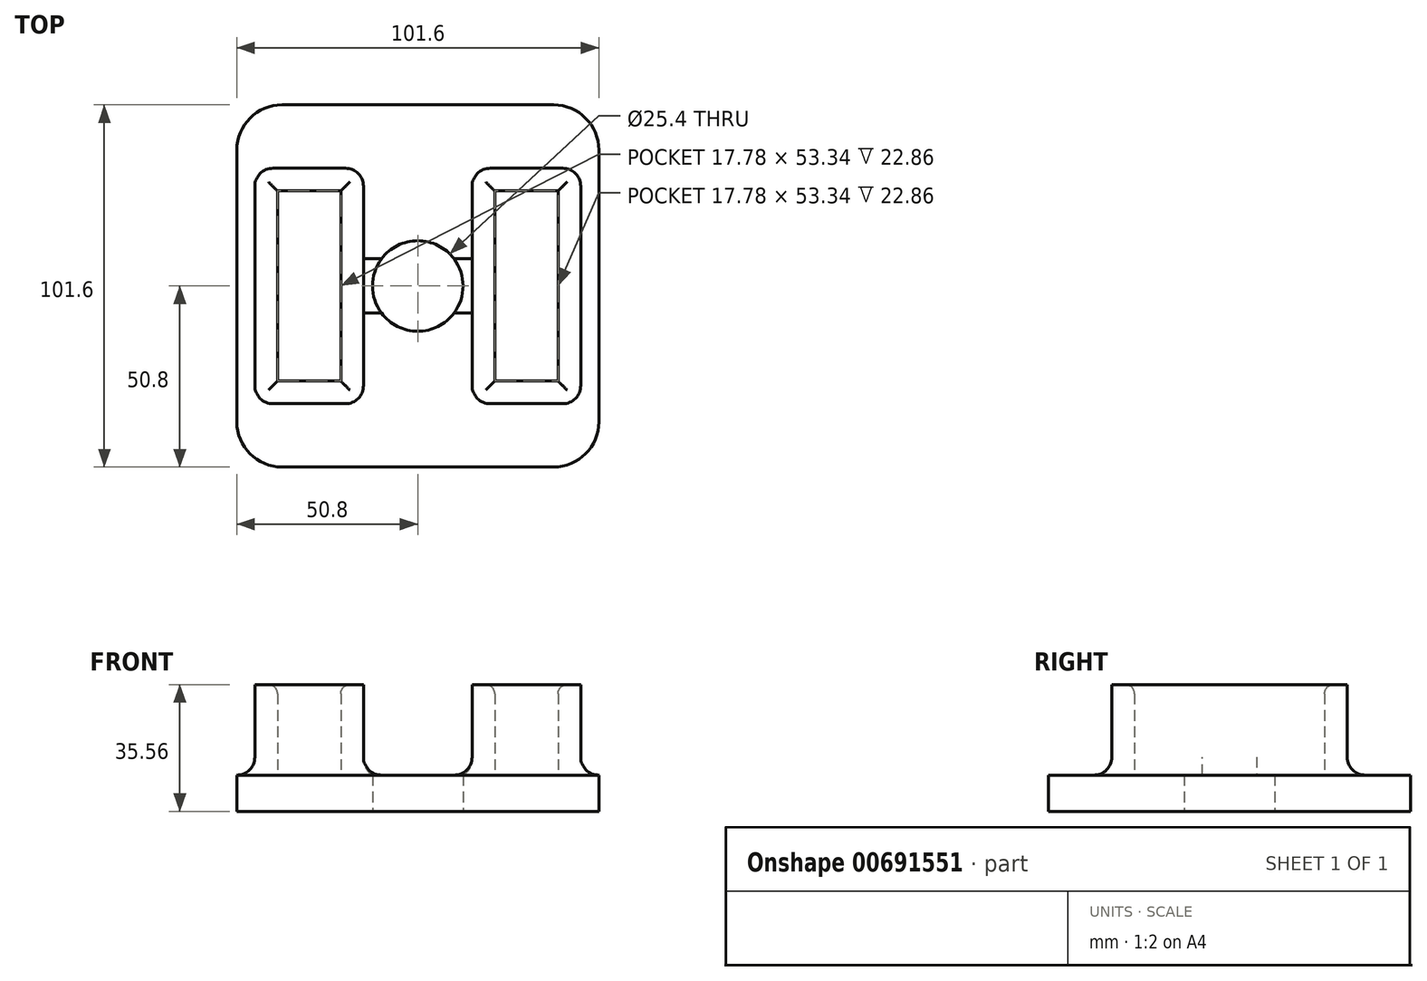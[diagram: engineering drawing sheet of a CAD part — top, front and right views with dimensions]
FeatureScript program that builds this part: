
annotation { "Feature Type Name" : "Feature", "Feature Type Description" : "" }
export const myFeature = defineFeature(function(context is Context, id is Id, definition is map)
    precondition{}
    {
        {
            var Q0;
            Q0=qCreatedBy(makeId("Top.planeOp"),FACE);
            var sketch = newSketch(context, id + "F0", { "sketchPlane" : qUnion([Q0])});
            skLineSegment(sketch, "E0.bottom", {"start": v(50.8, -50.8) * mm, "end": v(-50.8, -50.8) * mm});
            skLineSegment(sketch, "E0.top", {"start": v(50.8, 50.8) * mm, "end": v(-50.8, 50.8) * mm});
            skLineSegment(sketch, "E0.left", {"start": v(50.8, -50.8) * mm, "end": v(50.8, 50.8) * mm});
            skLineSegment(sketch, "E0.right", {"start": v(-50.8, -50.8) * mm, "end": v(-50.8, 50.8) * mm});
            skPoint(sketch, "E0.middle", {"position": v(0, 0) * mm});
            skCircle(sketch, "E1", {"center": v(0, 0) * mm, "radius": 12.7 * mm});
            skSolve(sketch);
        }
        {
            var Q0;
            Q0 = qSketchRegion(id + "F0", true);
            extrude(context, id + "F1", {"entities" : qUnion([Q0]), "depth" : 10.16 * mm, "offsetDistance" : 25.4 * mm});
        }
        {
            var Q0;
            Q0=makeQuery(id+"F1.opExtrude","CAP_FACE",FACE,{"disambiguationData":[OSD([sQuery(id+"F0.wireOp",EDGE,"E0.bottom"),sQuery(id+"F0.wireOp",EDGE,"E0.top"),sQuery(id+"F0.wireOp",EDGE,"E0.left"),sQuery(id+"F0.wireOp",EDGE,"E0.right"),sQuery(id+"F0.wireOp",EDGE,"E1")])],"isStart":false});
            var sketch = newSketch(context, id + "F2", { "sketchPlane" : qUnion([Q0])});
            skLineSegment(sketch, "E2", {"start": v(0, 0) * mm, "end": v(-30.48, 0) * mm});
            skLineSegment(sketch, "E3.bottom", {"start": v(-21.59, -26.67) * mm, "end": v(-39.37, -26.67) * mm});
            skLineSegment(sketch, "E3.top", {"start": v(-21.59, 26.67) * mm, "end": v(-39.37, 26.67) * mm});
            skLineSegment(sketch, "E3.left", {"start": v(-21.59, -26.67) * mm, "end": v(-21.59, 26.67) * mm});
            skLineSegment(sketch, "E3.right", {"start": v(-39.37, -26.67) * mm, "end": v(-39.37, 26.67) * mm});
            skPoint(sketch, "E3.middle", {"position": v(-30.48, 0) * mm});
            skLineSegment(sketch, "E4.bottom", {"start": v(-15.24, -33.02) * mm, "end": v(-45.72, -33.02) * mm});
            skLineSegment(sketch, "E4.top", {"start": v(-15.24, 33.02) * mm, "end": v(-45.72, 33.02) * mm});
            skLineSegment(sketch, "E4.left", {"start": v(-15.24, -33.02) * mm, "end": v(-15.24, 33.02) * mm});
            skLineSegment(sketch, "E4.right", {"start": v(-45.72, -33.02) * mm, "end": v(-45.72, 33.02) * mm});
            skLineSegment(sketch, "E5", {"start": v(0, 0) * mm, "end": v(0, 2.54) * mm});
            skPoint(sketch, "E6.MirrorP", {"position": v(30.48, 0) * mm});
            skLineSegment(sketch, "E7.MirrorCS", {"start": v(21.59, -26.67) * mm, "end": v(39.37, -26.67) * mm});
            skLineSegment(sketch, "E8.MirrorCS", {"start": v(45.72, -33.02) * mm, "end": v(45.72, 33.02) * mm});
            skLineSegment(sketch, "E9.MirrorCS", {"start": v(15.24, -33.02) * mm, "end": v(15.24, 33.02) * mm});
            skLineSegment(sketch, "E10.MirrorCS", {"start": v(21.59, 26.67) * mm, "end": v(39.37, 26.67) * mm});
            skLineSegment(sketch, "E11.MirrorCS", {"start": v(21.59, -26.67) * mm, "end": v(21.59, 26.67) * mm});
            skLineSegment(sketch, "E12.MirrorCS", {"start": v(39.37, -26.67) * mm, "end": v(39.37, 26.67) * mm});
            skLineSegment(sketch, "E13.MirrorCS", {"start": v(15.24, -33.02) * mm, "end": v(45.72, -33.02) * mm});
            skLineSegment(sketch, "E14.MirrorCS", {"start": v(15.24, 33.02) * mm, "end": v(45.72, 33.02) * mm});
            skLineSegment(sketch, "E15.MirrorCS", {"start": v(0, 0) * mm, "end": v(30.48, 0) * mm});
            skSolve(sketch);
        }
        {
            var Q0;
            {var subQ3=sQuery(id+"F2.wireOp",EDGE,"E3.bottom");Q0=makeQuery(id+"F2.imprint","IMPRINT",FACE,{"disambiguationData":[TD([[makeQuery(id+"F2.imprint","IMPRINT",EDGE,{"derivedFrom":subQ3}),1.0]])]});}
            var Q1;
            {var subQ4=sQuery(id+"F2.wireOp",EDGE,"E7.MirrorCS");Q1=makeQuery(id+"F2.imprint","IMPRINT",FACE,{"disambiguationData":[TD([[makeQuery(id+"F2.imprint","IMPRINT",EDGE,{"derivedFrom":subQ4}),-1.0]])]});}
            extrude(context, id + "F3", {"entities" : qUnion([Q0, Q1]), "operationType" : NewBodyOperationType.ADD, "depth" : 25.4 * mm, "offsetDistance" : 25.4 * mm});
        }
        {
            var Q0;
            Q0=makeQuery(id+"F1.opExtrude","SWEPT_EDGE",EDGE,{"disambiguationData":[OSD([sQuery(id+"F0.wireOp",EDGE,"E0.bottom"),sQuery(id+"F0.wireOp",EDGE,"E0.left")])]});
            var Q1;
            Q1=makeQuery(id+"F1.opExtrude","SWEPT_EDGE",EDGE,{"disambiguationData":[OSD([sQuery(id+"F0.wireOp",EDGE,"E0.bottom"),sQuery(id+"F0.wireOp",EDGE,"E0.right")])]});
            var Q2;
            Q2=makeQuery(id+"F1.opExtrude","SWEPT_EDGE",EDGE,{"disambiguationData":[OSD([sQuery(id+"F0.wireOp",EDGE,"E0.top"),sQuery(id+"F0.wireOp",EDGE,"E0.right")])]});
            var Q3;
            Q3=makeQuery(id+"F1.opExtrude","SWEPT_EDGE",EDGE,{"disambiguationData":[OSD([sQuery(id+"F0.wireOp",EDGE,"E0.top"),sQuery(id+"F0.wireOp",EDGE,"E0.left")])]});
            fillet(context, id + "F4", {"entities" : qUnion([Q0, Q1, Q2, Q3]), "radius" : 12.7 * mm, "tangentPropagation" : true, "allowEdgeOverflow" : false});
        }
        {
            var Q0;
            Q0=makeQuery(id+"F3.opExtrude","CAP_EDGE",EDGE,{"disambiguationData":[OSD([sQuery(id+"F2.wireOp",EDGE,"E3.right")])],"isStart":false});
            var Q1;
            Q1=makeQuery(id+"F3.opExtrude","CAP_EDGE",EDGE,{"disambiguationData":[OSD([sQuery(id+"F2.wireOp",EDGE,"E3.top")])],"isStart":false});
            var Q2;
            Q2=makeQuery(id+"F3.opExtrude","CAP_EDGE",EDGE,{"disambiguationData":[OSD([sQuery(id+"F2.wireOp",EDGE,"E3.bottom")])],"isStart":false});
            var Q3;
            Q3=makeQuery(id+"F3.opExtrude","CAP_EDGE",EDGE,{"disambiguationData":[OSD([sQuery(id+"F2.wireOp",EDGE,"E11.MirrorCS")])],"isStart":false});
            var Q4;
            Q4=makeQuery(id+"F3.opExtrude","CAP_EDGE",EDGE,{"disambiguationData":[OSD([sQuery(id+"F2.wireOp",EDGE,"E12.MirrorCS")])],"isStart":false});
            var Q5;
            Q5=makeQuery(id+"F3.opExtrude","CAP_EDGE",EDGE,{"disambiguationData":[OSD([sQuery(id+"F2.wireOp",EDGE,"E7.MirrorCS")])],"isStart":false});
            var Q6;
            Q6=makeQuery(id+"F3.opExtrude","CAP_EDGE",EDGE,{"disambiguationData":[OSD([sQuery(id+"F2.wireOp",EDGE,"E10.MirrorCS")])],"isStart":false});
            var Q7;
            Q7=makeQuery(id+"F3.opExtrude","CAP_EDGE",EDGE,{"disambiguationData":[OSD([sQuery(id+"F2.wireOp",EDGE,"E3.left")])],"isStart":false});
            fillet(context, id + "F5", {"entities" : qUnion([Q0, Q1, Q2, Q3, Q4, Q5, Q6, Q7]), "radius" : 2.54 * mm, "tangentPropagation" : true, "allowEdgeOverflow" : false});
        }
        {
            var Q0;
            Q0=makeQuery(id+"F3.opExtrude","CAP_EDGE",EDGE,{"disambiguationData":[OSD([sQuery(id+"F2.wireOp",EDGE,"E4.bottom")])],"isStart":true});
            var Q1;
            Q1=makeQuery(id+"F3.opExtrude","CAP_EDGE",EDGE,{"disambiguationData":[OSD([sQuery(id+"F2.wireOp",EDGE,"E4.right")])],"isStart":true});
            var Q2;
            Q2=makeQuery(id+"F3.opExtrude","CAP_EDGE",EDGE,{"disambiguationData":[OSD([sQuery(id+"F2.wireOp",EDGE,"E4.left")])],"isStart":true});
            var Q3;
            Q3=makeQuery(id+"F3.opExtrude","CAP_EDGE",EDGE,{"disambiguationData":[OSD([sQuery(id+"F2.wireOp",EDGE,"E9.MirrorCS")])],"isStart":true});
            var Q4;
            Q4=makeQuery(id+"F3.opExtrude","CAP_EDGE",EDGE,{"disambiguationData":[OSD([sQuery(id+"F2.wireOp",EDGE,"E13.MirrorCS")])],"isStart":true});
            var Q5;
            Q5=makeQuery(id+"F3.opExtrude","CAP_EDGE",EDGE,{"disambiguationData":[OSD([sQuery(id+"F2.wireOp",EDGE,"E8.MirrorCS")])],"isStart":true});
            var Q6;
            Q6=makeQuery(id+"F3.opExtrude","CAP_EDGE",EDGE,{"disambiguationData":[OSD([sQuery(id+"F2.wireOp",EDGE,"E14.MirrorCS")])],"isStart":true});
            var Q7;
            Q7=makeQuery(id+"F3.opExtrude","CAP_EDGE",EDGE,{"disambiguationData":[OSD([sQuery(id+"F2.wireOp",EDGE,"E4.top")])],"isStart":true});
            var Q8;
            Q8=makeQuery(id+"F3.opExtrude","SWEPT_EDGE",EDGE,{"disambiguationData":[OSD([sQuery(id+"F2.wireOp",EDGE,"E4.top"),sQuery(id+"F2.wireOp",EDGE,"E4.left")])]});
            var Q9;
            Q9=makeQuery(id+"F3.opExtrude","SWEPT_EDGE",EDGE,{"disambiguationData":[OSD([sQuery(id+"F2.wireOp",EDGE,"E4.top"),sQuery(id+"F2.wireOp",EDGE,"E4.right")])]});
            var Q10;
            Q10=makeQuery(id+"F3.opExtrude","SWEPT_EDGE",EDGE,{"disambiguationData":[OSD([sQuery(id+"F2.wireOp",EDGE,"E4.bottom"),sQuery(id+"F2.wireOp",EDGE,"E4.right")])]});
            var Q11;
            Q11=makeQuery(id+"F3.opExtrude","SWEPT_EDGE",EDGE,{"disambiguationData":[OSD([sQuery(id+"F2.wireOp",EDGE,"E4.bottom"),sQuery(id+"F2.wireOp",EDGE,"E4.left")])]});
            var Q12;
            Q12=makeQuery(id+"F3.opExtrude","SWEPT_EDGE",EDGE,{"disambiguationData":[OSD([sQuery(id+"F2.wireOp",EDGE,"E9.MirrorCS"),sQuery(id+"F2.wireOp",EDGE,"E13.MirrorCS")])]});
            var Q13;
            Q13=makeQuery(id+"F3.opExtrude","SWEPT_EDGE",EDGE,{"disambiguationData":[OSD([sQuery(id+"F2.wireOp",EDGE,"E8.MirrorCS"),sQuery(id+"F2.wireOp",EDGE,"E13.MirrorCS")])]});
            var Q14;
            Q14=makeQuery(id+"F3.opExtrude","SWEPT_EDGE",EDGE,{"disambiguationData":[OSD([sQuery(id+"F2.wireOp",EDGE,"E9.MirrorCS"),sQuery(id+"F2.wireOp",EDGE,"E14.MirrorCS")])]});
            var Q15;
            Q15=makeQuery(id+"F3.opExtrude","SWEPT_EDGE",EDGE,{"disambiguationData":[OSD([sQuery(id+"F2.wireOp",EDGE,"E8.MirrorCS"),sQuery(id+"F2.wireOp",EDGE,"E14.MirrorCS")])]});
            fillet(context, id + "F6", {"entities" : qUnion([Q0, Q1, Q2, Q3, Q4, Q5, Q6, Q7, Q8, Q9, Q10, Q11, Q12, Q13, Q14, Q15]), "radius" : 5.08 * mm, "tangentPropagation" : true, "allowEdgeOverflow" : false});
        }
    });
